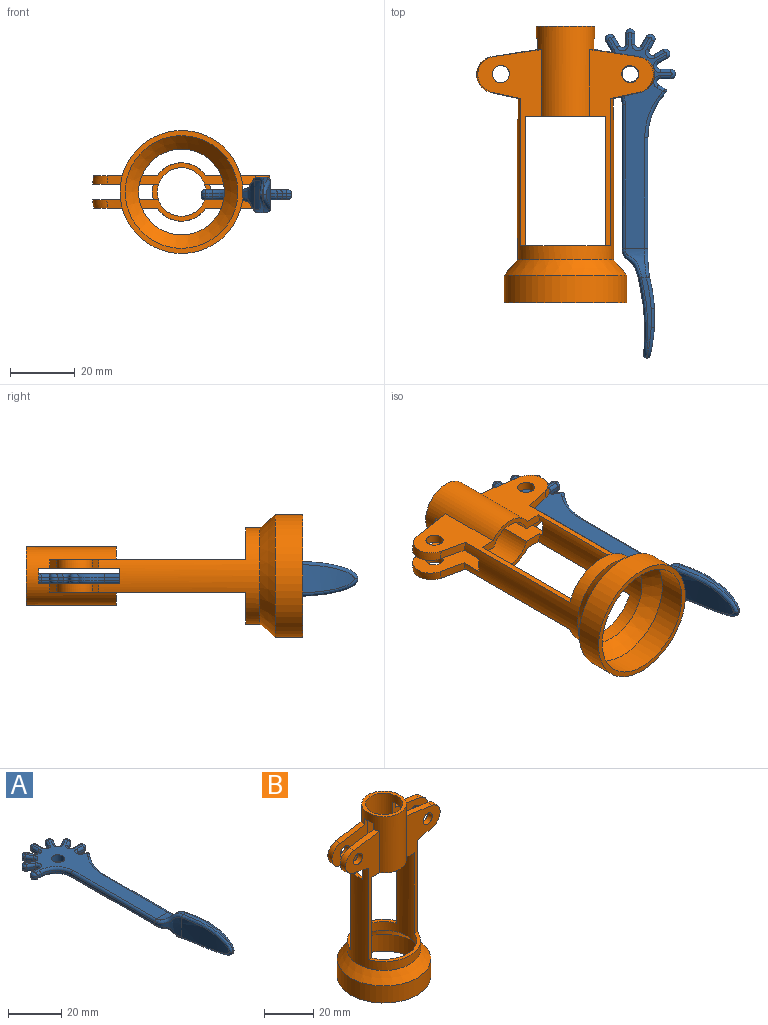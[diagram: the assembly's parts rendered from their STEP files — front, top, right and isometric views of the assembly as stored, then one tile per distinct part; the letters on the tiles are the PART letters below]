
ASSEMBLY  parts=2 mates=1
PART A: 135 faces, bbox 28x102x11.2 mm
  f0: bspline ~11.28x5.09mm, area 16.1mm2, adj f1,f45,f49,f132
  f1: bspline ~11.45x5.84mm, area 16mm2, adj f0,f44,f49,f134
  f2: plane 67x26mm, normal (0,0,1), area 500mm2, adj f39,f40,f54,f56,f58,f60,f62,f64
  f3: plane 67x26mm, normal (0,0,-1), area 500.1mm2, adj f39,f43,f59,f61,f63,f65,f67,f69
  f4: plane 34.31x1mm, normal (1,0,0), area 34.3mm2, adj f5,f42,f122,f127
  f5: cylinder r=20mm len=12.21mm, axis (0,0,-1), area 13.1mm2, adj f4,f6,f120,f125
  f6: plane 2.04x1.57mm, normal (0.79,-0.61,0), area 2.6mm2, adj f5,f7,f118,f123
  f7: cylinder r=0.5mm len=1mm, axis (0,0,-1), area 0.9mm2, adj f6,f8,f116,f121
  f8: plane 2.35x1.36mm, normal (0.5,0.87,0), area 2.7mm2, adj f7,f9,f114,f119
  f9: cylinder r=1mm len=1.87mm, axis (0,0,-1), area 2.6mm2, adj f8,f10,f112,f117
  f10: plane 3.29x1mm, normal (0,-1,0), area 3.3mm2, adj f9,f11,f110,f115
  f11: cylinder r=1.47mm len=2.95mm, axis (0,0,-1), area 4.6mm2, adj f10,f12,f108,f113
  f12: plane 3.29x1mm, normal (0,1,0), area 3.3mm2, adj f11,f13,f106,f111
  f13: cylinder r=1mm len=1.87mm, axis (0,0,-1), area 2.6mm2, adj f12,f14,f104,f109
  f14: plane 2.85x1.64mm, normal (0.5,-0.87,0), area 3.3mm2, adj f13,f15,f102,f107
  f15: cylinder r=1.47mm len=2.75mm, axis (0,0,-1), area 4.6mm2, adj f14,f16,f100,f105
  f16: plane 2.85x1.64mm, normal (-0.5,0.87,0), area 3.3mm2, adj f15,f17,f98,f103
  f17: cylinder r=1mm len=1.5mm, axis (0,0,-1), area 2.6mm2, adj f16,f18,f96,f101
  f18: plane 2.85x1.64mm, normal (0.87,-0.5,0), area 3.3mm2, adj f17,f19,f94,f99
  f19: cylinder r=1.47mm len=2.75mm, axis (0,0,-1), area 4.6mm2, adj f18,f20,f92,f97
  f20: plane 2.85x1.64mm, normal (-0.87,0.5,0), area 3.3mm2, adj f19,f21,f90,f95
  f21: cylinder r=1mm len=1.87mm, axis (0,0,-1), area 2.6mm2, adj f20,f22,f88,f93
  f22: plane 3.29x1mm, normal (1,0,0), area 3.3mm2, adj f21,f23,f86,f91
  f23: cylinder r=1.47mm len=2.95mm, axis (0,0,-1), area 4.6mm2, adj f22,f24,f84,f89
  f24: plane 3.29x1mm, normal (-1,0,0), area 3.3mm2, adj f23,f25,f82,f87
  f25: cylinder r=1mm len=1.87mm, axis (0,0,-1), area 2.6mm2, adj f24,f26,f80,f85
  f26: plane 2.85x1.64mm, normal (0.87,0.5,0), area 3.3mm2, adj f25,f27,f78,f83
  f27: cylinder r=1.47mm len=2.75mm, axis (0,0,-1), area 4.6mm2, adj f26,f28,f76,f81
  f28: plane 2.85x1.64mm, normal (-0.87,-0.5,0), area 3.3mm2, adj f27,f29,f74,f79
  f29: cylinder r=1mm len=1.5mm, axis (0,0,-1), area 2.6mm2, adj f28,f30,f72,f77
  f30: plane 2.85x1.64mm, normal (0.5,0.87,0), area 3.3mm2, adj f29,f31,f70,f75
  f31: cylinder r=1.47mm len=2.75mm, axis (0,0,-1), area 4.6mm2, adj f30,f32,f68,f73
  f32: plane 2.85x1.64mm, normal (-0.5,-0.87,0), area 3.3mm2, adj f31,f33,f66,f71
  f33: cylinder r=1mm len=1.87mm, axis (0,0,-1), area 2.6mm2, adj f32,f34,f64,f69
  f34: plane 3.29x1mm, normal (0,1,0), area 3.3mm2, adj f33,f35,f62,f67
  f35: cylinder r=1.47mm len=2.95mm, axis (0,0,-1), area 4.6mm2, adj f34,f36,f60,f65
  f36: plane 2.03x1mm, normal (0,-1,0), area 2mm2, adj f35,f37,f58,f63
  f37: cylinder r=8mm len=8mm, axis (0,0,-1), area 12.6mm2, adj f36,f38,f56,f61
  f38: plane 44.53x1mm, normal (-1,0,0), area 44.5mm2, adj f37,f41,f54,f59
  f39: cylinder r=2.5mm len=5mm, axis (0,0,-1), area 47.1mm2, adj f2,f3
  f40: bspline ~9x8.5mm, area 32mm2, adj f2,f45,f50,f126
  f41: bspline ~11.04x9.17mm, area 41.6mm2, adj f38,f47,f50,f52,f53,f55,f57
  f42: bspline ~11.18x9mm, area 41.6mm2, adj f4,f48,f124,f126,f128,f129,f131
  f43: bspline ~9.16x8.53mm, area 31.9mm2, adj f3,f44,f53,f55,f131,f133
  f44: extruded ~25x5.5mm, area 26.5mm2, adj f1,f43,f45,f53,f133,f134
  f45: extruded ~25x5.5mm, area 26.5mm2, adj f0,f40,f44,f50,f51,f128,f130,f132
  f46: plane 8.62x5.93mm, normal (1,0,0), area 47.9mm2, adj f48,f49,f130,f132,f134
  f47: cylinder r=70mm len=23.9mm, axis (0,0,1), area 177mm2, adj f41,f50,f51,f53
  f48: cylinder r=50mm len=9.54mm, axis (0,0,1), area 86mm2, adj f42,f46,f130,f131,f133
  f49: cylinder r=50mm len=8.77mm, axis (0,0,1), area 44.8mm2, adj f0,f1,f46,f134
  f50: bspline ~10.14x6.08mm, area 21.2mm2, adj f40,f41,f45,f47,f51,f52
  f51: bspline ~28.39x5.54mm, area 41.4mm2, adj f45,f47,f50,f53
  f52: bspline ~2.18x1.06mm, area 0mm2, adj f41,f50,f54
  f53: bspline ~28.39x5.54mm, area 41.4mm2, adj f41,f43,f44,f47,f51,f55
  f54: cylinder r=1mm len=44.53mm, axis (0,-1,0), area 69.9mm2, adj f2,f38,f52,f56
  f55: bspline ~9.7x6.12mm, area 21mm2, adj f41,f43,f53,f57
  f56: torus R=9mm, axis (0,0,-1), area 20.6mm2, adj f2,f37,f54,f58
  f57: bspline ~3.31x1.02mm, area 0.1mm2, adj f41,f55,f59
  f58: cylinder r=1mm len=2.03mm, axis (1,0,0), area 3.2mm2, adj f2,f36,f56,f60
  f59: cylinder r=1mm len=44.53mm, axis (0,1,0), area 69.9mm2, adj f3,f38,f57,f61
  f60: torus R=0.47mm, axis (0,0,-1), area 5.5mm2, adj f2,f35,f58,f62
  f61: torus R=9mm, axis (0,0,-1), area 20.6mm2, adj f3,f37,f59,f63
  f62: cylinder r=1mm len=3.29mm, axis (-1,0,0), area 5.2mm2, adj f2,f34,f60,f64
  f63: cylinder r=1mm len=2.03mm, axis (-1,0,0), area 3.2mm2, adj f3,f36,f61,f65
  f64: torus R=2mm, axis (0,0,-1), area 5.6mm2, adj f2,f33,f62,f66
  f65: torus R=0.47mm, axis (0,0,-1), area 5.5mm2, adj f3,f35,f63,f67
  f66: cylinder r=1mm len=3.35mm, axis (0.87,-0.5,0), area 5.2mm2, adj f2,f32,f64,f68
  f67: cylinder r=1mm len=3.29mm, axis (1,0,0), area 5.2mm2, adj f3,f34,f65,f69
  f68: torus R=0.47mm, axis (0,0,-1), area 5.5mm2, adj f2,f31,f66,f70
  f69: torus R=2mm, axis (0,0,-1), area 5.6mm2, adj f3,f33,f67,f71
  f70: cylinder r=1mm len=3.35mm, axis (-0.87,0.5,0), area 5.2mm2, adj f2,f30,f68,f72
  f71: cylinder r=1mm len=3.35mm, axis (-0.87,0.5,0), area 5.2mm2, adj f3,f32,f69,f73
  f72: torus R=2mm, axis (0,0,-1), area 5.6mm2, adj f2,f29,f70,f74
  f73: torus R=0.47mm, axis (0,0,-1), area 5.5mm2, adj f3,f31,f71,f75
  f74: cylinder r=1mm len=3.35mm, axis (0.5,-0.87,0), area 5.2mm2, adj f2,f28,f72,f76
  f75: cylinder r=1mm len=3.35mm, axis (0.87,-0.5,0), area 5.2mm2, adj f3,f30,f73,f77
  f76: torus R=0.47mm, axis (0,0,-1), area 5.5mm2, adj f2,f27,f74,f78
  f77: torus R=2mm, axis (0,0,-1), area 5.6mm2, adj f3,f29,f75,f79
  f78: cylinder r=1mm len=3.35mm, axis (-0.5,0.87,0), area 5.2mm2, adj f2,f26,f76,f80
  f79: cylinder r=1mm len=3.35mm, axis (-0.5,0.87,0), area 5.2mm2, adj f3,f28,f77,f81
  f80: torus R=2mm, axis (0,0,-1), area 5.6mm2, adj f2,f25,f78,f82
  f81: torus R=0.47mm, axis (0,0,-1), area 5.5mm2, adj f3,f27,f79,f83
  f82: cylinder r=1mm len=3.29mm, axis (0,-1,0), area 5.2mm2, adj f2,f24,f80,f84
  f83: cylinder r=1mm len=3.35mm, axis (0.5,-0.87,0), area 5.2mm2, adj f3,f26,f81,f85
  f84: torus R=0.47mm, axis (0,0,-1), area 5.5mm2, adj f2,f23,f82,f86
  f85: torus R=2mm, axis (0,0,-1), area 5.6mm2, adj f3,f25,f83,f87
  f86: cylinder r=1mm len=3.29mm, axis (0,1,0), area 5.2mm2, adj f2,f22,f84,f88
  f87: cylinder r=1mm len=3.29mm, axis (0,1,0), area 5.2mm2, adj f3,f24,f85,f89
  f88: torus R=2mm, axis (0,0,-1), area 5.6mm2, adj f2,f21,f86,f90
  f89: torus R=0.47mm, axis (0,0,-1), area 5.5mm2, adj f3,f23,f87,f91
  f90: cylinder r=1mm len=3.35mm, axis (-0.5,-0.87,0), area 5.2mm2, adj f2,f20,f88,f92
  f91: cylinder r=1mm len=3.29mm, axis (0,-1,0), area 5.2mm2, adj f3,f22,f89,f93
  f92: torus R=0.47mm, axis (0,0,-1), area 5.5mm2, adj f2,f19,f90,f94
  f93: torus R=2mm, axis (0,0,-1), area 5.6mm2, adj f3,f21,f91,f95
  f94: cylinder r=1mm len=3.35mm, axis (0.5,0.87,0), area 5.2mm2, adj f2,f18,f92,f96
  f95: cylinder r=1mm len=3.35mm, axis (0.5,0.87,0), area 5.2mm2, adj f3,f20,f93,f97
  f96: torus R=2mm, axis (0,0,-1), area 5.6mm2, adj f2,f17,f94,f98
  f97: torus R=0.47mm, axis (0,0,-1), area 5.5mm2, adj f3,f19,f95,f99
  f98: cylinder r=1mm len=3.35mm, axis (-0.87,-0.5,0), area 5.2mm2, adj f2,f16,f96,f100
  f99: cylinder r=1mm len=3.35mm, axis (-0.5,-0.87,0), area 5.2mm2, adj f3,f18,f97,f101
  f100: torus R=0.47mm, axis (0,0,-1), area 5.5mm2, adj f2,f15,f98,f102
  f101: torus R=2mm, axis (0,0,-1), area 5.6mm2, adj f3,f17,f99,f103
  f102: cylinder r=1mm len=3.35mm, axis (0.87,0.5,0), area 5.2mm2, adj f2,f14,f100,f104
  f103: cylinder r=1mm len=3.35mm, axis (0.87,0.5,0), area 5.2mm2, adj f3,f16,f101,f105
  f104: torus R=2mm, axis (0,0,-1), area 5.6mm2, adj f2,f13,f102,f106
  f105: torus R=0.47mm, axis (0,0,-1), area 5.5mm2, adj f3,f15,f103,f107
  f106: cylinder r=1mm len=3.29mm, axis (-1,0,0), area 5.2mm2, adj f2,f12,f104,f108
  f107: cylinder r=1mm len=3.35mm, axis (-0.87,-0.5,0), area 5.2mm2, adj f3,f14,f105,f109
  f108: torus R=0.47mm, axis (0,0,-1), area 5.5mm2, adj f2,f11,f106,f110
  f109: torus R=2mm, axis (0,0,-1), area 5.6mm2, adj f3,f13,f107,f111
  f110: cylinder r=1mm len=3.29mm, axis (1,0,0), area 5.2mm2, adj f2,f10,f108,f112
  f111: cylinder r=1mm len=3.29mm, axis (1,0,0), area 5.2mm2, adj f3,f12,f109,f113
  f112: torus R=2mm, axis (0,0,-1), area 5.6mm2, adj f2,f9,f110,f114
  f113: torus R=0.47mm, axis (0,0,-1), area 5.5mm2, adj f3,f11,f111,f115
  f114: cylinder r=1mm len=2.85mm, axis (-0.87,0.5,0), area 3.8mm2, adj f2,f8,f112,f116
  f115: cylinder r=1mm len=3.29mm, axis (-1,0,0), area 5.2mm2, adj f3,f10,f113,f117
  f116: bspline ~1.49x1.05mm, area 0.6mm2, adj f7,f114,f118
  f117: torus R=2mm, axis (0,0,-1), area 5.6mm2, adj f3,f9,f115,f119
  f118: cylinder r=1mm len=2.65mm, axis (0.61,0.79,0), area 3.6mm2, adj f2,f6,f116,f120
  f119: cylinder r=1mm len=2.85mm, axis (0.87,-0.5,0), area 3.8mm2, adj f3,f8,f117,f121
  f120: torus R=21mm, axis (0,0,-1), area 21mm2, adj f2,f5,f118,f122
  f121: bspline ~1.49x1.05mm, area 0.6mm2, adj f7,f119,f123
  f122: cylinder r=1mm len=34.31mm, axis (0,1,0), area 53.9mm2, adj f2,f4,f120,f124
  f123: cylinder r=1mm len=2.65mm, axis (-0.61,-0.79,0), area 3.6mm2, adj f3,f6,f121,f125
  f124: bspline ~5.84x1.06mm, area 0mm2, adj f42,f122,f126
  f125: torus R=21mm, axis (0,0,-1), area 21mm2, adj f3,f5,f123,f127
  f126: bspline ~10.63x5.03mm, area 15.8mm2, adj f40,f42,f124,f128
  f127: cylinder r=1mm len=34.31mm, axis (0,-1,0), area 53.9mm2, adj f3,f4,f125,f129
  f128: bspline ~4.36x1.58mm, area 0.3mm2, adj f42,f45,f126,f130
  f129: bspline ~5.84x1.03mm, area 0.1mm2, adj f42,f127,f131
  f130: bspline ~12.68x2.94mm, area 15.2mm2, adj f45,f46,f48,f128,f132
  f131: bspline ~9.76x5.04mm, area 15.9mm2, adj f42,f43,f48,f129,f133
  f132: bspline ~10.7x2.4mm, area 9.4mm2, adj f0,f45,f46,f130
  f133: bspline ~12.68x2.94mm, area 15.3mm2, adj f43,f44,f48,f131,f134
  f134: bspline ~10.45x2mm, area 9.4mm2, adj f1,f44,f46,f49,f133
PART B: 42 faces, bbox 56.4x39.3x87 mm
  f0: cone r=14.9mm half-angle=77deg, axis (0,0,1), area 24.9mm2, adj f2,f15,f24,f36
  f1: cone r=14.9mm half-angle=77deg, axis (0,0,1), area 24.9mm2, adj f3,f15,f25,f31
  f2: torus R=22.02mm, axis (0,0,-1), area 43.1mm2, adj f0,f4,f24,f36
  f3: torus R=22.02mm, axis (0,0,-1), area 43.1mm2, adj f1,f5,f25,f31
  f4: cone r=9.05mm half-angle=81.1deg, axis (0,0,-1), area 34.5mm2, adj f2,f16,f24,f36
  f5: cone r=9.05mm half-angle=81.1deg, axis (0,0,-1), area 34.5mm2, adj f3,f16,f25,f31
  f6: plane 26.18x6.68mm, normal (0,0,-1), area 56.7mm2, adj f14,f16,f18,f24,f25,f31,f36
  f7: cone r=14.9mm half-angle=77deg, axis (0,0,1), area 24.4mm2, adj f9,f15,f27,f35
  f8: cone r=14.9mm half-angle=77deg, axis (0,0,1), area 24.4mm2, adj f10,f15,f28,f32
  f9: torus R=22.02mm, axis (0,0,-1), area 42mm2, adj f7,f11,f27,f35
  f10: torus R=22.02mm, axis (0,0,-1), area 42mm2, adj f8,f12,f28,f32
  f11: cone r=9.05mm half-angle=81.1deg, axis (0,0,-1), area 33.4mm2, adj f9,f16,f27,f35
  f12: cone r=9.05mm half-angle=81.1deg, axis (0,0,-1), area 33.4mm2, adj f10,f16,f28,f32
  f13: plane 26.15x6.62mm, normal (0,0,-1), area 56mm2, adj f14,f16,f18,f27,f28,f32,f35
  f14: cylinder r=13.3mm len=44.5mm, axis (0,0,-1), area 1197.6mm2, adj f6,f13,f19,f24,f25,f26,f27,f28
  f15: cylinder r=14.9mm len=50mm, axis (0,0,-1), area 1298.7mm2, adj f0,f1,f7,f8,f23,f24,f25,f26
  f16: cylinder r=9.05mm len=28mm, axis (0,0,-1), area 1111.5mm2, adj f4,f5,f6,f11,f12,f13,f17,f24
  f17: plane 18.1x18.1mm, normal (0,0,1), area 78.2mm2, adj f16,f18
  f18: cylinder r=7.55mm len=28mm, axis (0,0,-1), area 1093.8mm2, adj f6,f13,f17,f30,f31,f32,f35,f36
  f19: cone r=17.45mm half-angle=40.8deg, axis (0,0,-1), area 613mm2, adj f14,f20
  f20: cylinder r=17.45mm len=34.9mm, axis (0,0,-1), area 932mm2, adj f19,f21
  f21: plane 38.1x38.1mm, normal (0,0,-1), area 183.5mm2, adj f20,f22
  f22: cylinder r=19.05mm len=38.1mm, axis (0,0,-1), area 1017.4mm2, adj f21,f23
  f23: cone r=19.05mm half-angle=40.8deg, axis (0,0,-1), area 676.8mm2, adj f15,f22
  f24: plane 61.35x20.27mm, normal (0,1,0), area 326mm2, adj f0,f2,f4,f6,f14,f15,f16,f26
  f25: plane 61.35x20.27mm, normal (0,1,0), area 326mm2, adj f1,f3,f5,f6,f14,f15,f16,f26
  f26: plane 28x9.8mm, normal (0,0,1), area 54.2mm2, adj f14,f15,f24,f25
  f27: plane 61.35x20.27mm, normal (0,-1,0), area 326mm2, adj f7,f9,f11,f13,f14,f15,f16,f29
  f28: plane 61.35x20.27mm, normal (0,-1,0), area 326mm2, adj f8,f10,f12,f13,f14,f15,f16,f29
  f29: plane 28x9.8mm, normal (0,0,1), area 54.2mm2, adj f14,f15,f27,f28
  f30: plane 4.8x1.9mm, normal (0,0,-1), area 7.3mm2, adj f16,f18,f31,f32
  f31: plane 26.12x21.52mm, normal (0,-1,0), area 281.2mm2, adj f1,f3,f5,f6,f14,f15,f16,f18
  f32: plane 26.15x21.57mm, normal (0,1,0), area 281.5mm2, adj f8,f10,f12,f13,f14,f15,f16,f18
  f33: plane 4.8x1.82mm, normal (0,0,1), area 7.7mm2, adj f14,f15,f31,f32
  f34: plane 4.8x1.82mm, normal (0,0,1), area 7.7mm2, adj f14,f15,f35,f36
  f35: plane 26.15x21.57mm, normal (0,1,0), area 281.5mm2, adj f7,f9,f11,f13,f14,f15,f16,f18
  f36: plane 26.12x21.52mm, normal (0,-1,0), area 281.2mm2, adj f0,f2,f4,f6,f14,f15,f16,f18
  f37: plane 4.8x1.9mm, normal (0,0,-1), area 7.3mm2, adj f16,f18,f35,f36
  f38: cylinder r=2.65mm len=5.3mm, axis (0,1,0), area 45.5mm2, adj f24,f36
  f39: cylinder r=2.65mm len=5.3mm, axis (0,1,0), area 44.4mm2, adj f27,f35
  f40: cylinder r=2.65mm len=5.3mm, axis (0,1,0), area 44.4mm2, adj f28,f32
  f41: cylinder r=2.65mm len=5.3mm, axis (0,1,0), area 45.5mm2, adj f25,f31
PLACE A t=(-54.35,54.48,42.83)mm
PLACE B rot(axis=(-1,0,0),90deg) t=(-74.4,-16.42,43.69)mm
MATE revolute B.f38 <-> A.f39  axis (0,0,1) through (-54.35,54.48,41.33)mm
